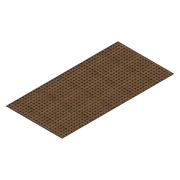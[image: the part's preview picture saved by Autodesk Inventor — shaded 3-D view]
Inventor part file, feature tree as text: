
AUTODESK INVENTOR PART (.ipt)
format: ipt  version: 2020.2 (Build 242310000, 310)  size: 110,592 bytes
history: native  units: mm
features: extrude x1, sketch x1
ambient origin geometry x8: Origin, YZ Plane, XZ Plane, XY Plane, X Axis, Y Axis, Z Axis, Center Point
bodies: Solid1 (feature_tree)
feature tree (2):
  extrude  "Extrusion1"  Depth=2000.0mm
  sketch  "Sketch1"  dims[d0=1000.0mm d1=2000.0mm d2=3.0mm d3=0.0mm]
